# Revit family: Martin Brattrud - Medinah - Chair - Arms - Full
name_source: partatom
category: Furniture
revit_build: Autodesk Revit LT 2016 (Build: 20151007_0715(x64)
units: mm (PartAtom-declared; Revit-internal decimal feet)

## family parameters
Always vertical = Yes
Cut with Voids When Loaded = No
OmniClass Number = 23.40.20.00
OmniClass Title = General Furniture and Specialties
Room Calculation Point = No
Shared = No
Work Plane-Based = No

## types (6) — shared parameters
Assembly Code = E2020200
DEPTH = 2' - 4"
Description = Medinah Chair, Arms
Keynote = 125000
Leg Offset = 0' - 5"
Manufacturer = Martin Brattrud, Inc.
SCS Certified Product = Yes
URL = http://www.martinbrattrud.com

## per-type parameters (varying)
| type | HEIGHT | Model | WIDTH |
| Low Back | 2' - 9" | 1924-28 | 3' - 6" |
| Mid Back | 3' - 7" | 1925-28 | 3' - 6" |
| High Back | 4' - 6" | 1926-28 | 3' - 6" |
| Low Back, Wide | 2' - 9" | 1924-38 | 3' - 10" |
| Mid Back, Wide | 3' - 7" | 1925-38 | 3' - 10" |
| High Back, Wide | 4' - 6" | 1926-38 | 3' - 10" |

## geometry (parser evidence)
native form markers: Sweep x12
no freeform markers — native parametric forms only
